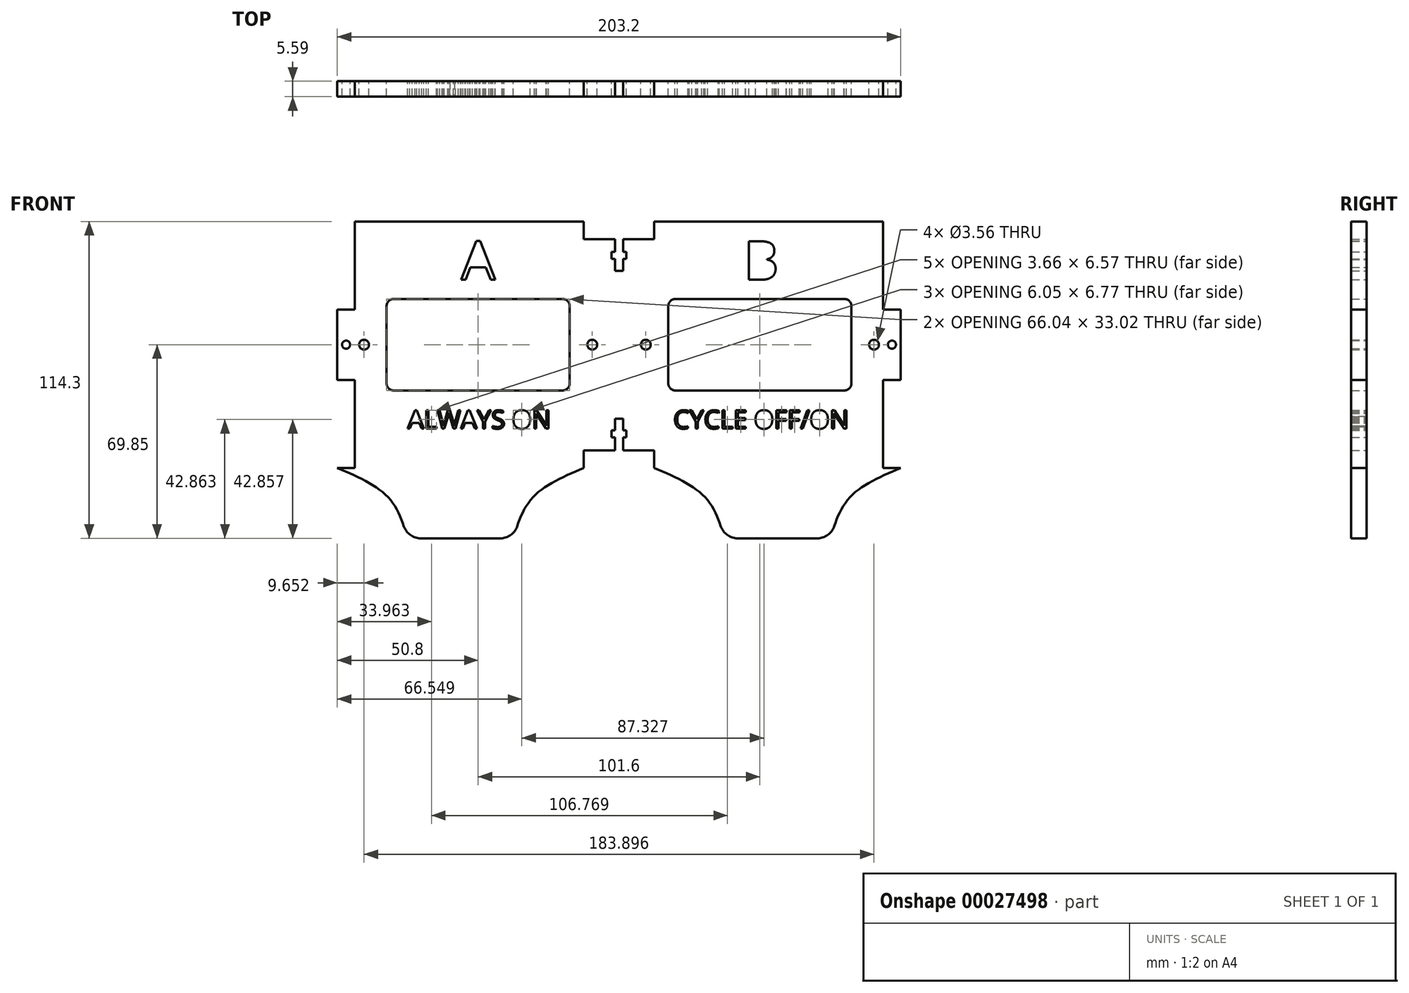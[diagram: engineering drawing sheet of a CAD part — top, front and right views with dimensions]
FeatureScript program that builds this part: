
annotation { "Feature Type Name" : "Feature", "Feature Type Description" : "" }
export const myFeature = defineFeature(function(context is Context, id is Id, definition is map)
    precondition{}
    {
        {
            var Q0;
            Q0=qCreatedBy(makeId("Front.planeOp"),FACE);
            var sketch = newSketch(context, id + "F0", { "sketchPlane" : qUnion([Q0])});
            skLineSegment(sketch, "E0.rect.bottom", {"start": v(95.25, 44.45) * mm, "end": v(12.7, 44.45) * mm});
            skLineSegment(sketch, "E0.rect.left", {"start": v(101.6, 12.7) * mm, "end": v(101.6, -12.7) * mm});
            skPoint(sketch, "E0.rect.middle", {"position": v(0, 0) * mm});
            skLineSegment(sketch, "E1", {"start": v(0, 44.45) * mm, "end": v(0, -44.45) * mm, "construction": true});
            skLineSegment(sketch, "E2", {"start": v(0, 0) * mm, "end": v(95.25, 0) * mm, "construction": true});
            skPoint(sketch, "E3.orphan", {"position": v(-101.6, 0) * mm});
            skLineSegment(sketch, "E4", {"start": v(0, 0) * mm, "end": v(-101.6, 0) * mm, "construction": true});
            skLineSegment(sketch, "E5.rect.bottom", {"start": v(-20.32, -16.51) * mm, "end": v(-81.28, -16.51) * mm});
            skLineSegment(sketch, "E5.rect.top", {"start": v(-20.32, 16.5) * mm, "end": v(-81.28, 16.5) * mm});
            skLineSegment(sketch, "E5.rect.left", {"start": v(-17.78, -13.97) * mm, "end": v(-17.78, 13.97) * mm});
            skLineSegment(sketch, "E5.rect.right", {"start": v(-83.82, -13.97) * mm, "end": v(-83.82, 13.97) * mm});
            skPoint(sketch, "E5.rect.middle", {"position": v(-50.8, 0) * mm});
            skPoint(sketch, "E6.visualSharp", {"position": v(-17.78, 16.51) * mm});
            skArc(sketch, "E6.filletArc", {"start": v(-17.78, 13.97) * mm, "mid": v(-18.52, 15.77) * mm, "end": v(-20.32, 16.5) * mm});
            skPoint(sketch, "E7.visualSharp", {"position": v(-83.82, 16.51) * mm});
            skArc(sketch, "E7.filletArc", {"start": v(-81.28, 16.5) * mm, "mid": v(-83.08, 15.77) * mm, "end": v(-83.82, 13.97) * mm});
            skPoint(sketch, "E8.visualSharp", {"position": v(-83.82, -16.51) * mm});
            skArc(sketch, "E8.filletArc", {"start": v(-83.82, -13.97) * mm, "mid": v(-83.08, -15.77) * mm, "end": v(-81.28, -16.5) * mm});
            skPoint(sketch, "E9.visualSharp", {"position": v(-17.78, -16.51) * mm});
            skArc(sketch, "E9.filletArc", {"start": v(-20.32, -16.51) * mm, "mid": v(-18.52, -15.77) * mm, "end": v(-17.78, -13.97) * mm});
            skCircle(sketch, "E10", {"center": v(-91.95, 0) * mm, "radius": 1.78 * mm});
            skCircle(sketch, "E11", {"center": v(-9.65, 0) * mm, "radius": 1.78 * mm});
            skLineSegment(sketch, "E12.MirrorCS", {"start": v(20.32, 16.5) * mm, "end": v(81.28, 16.5) * mm});
            skLineSegment(sketch, "E13.MirrorCS", {"start": v(83.82, -13.97) * mm, "end": v(83.82, 13.97) * mm});
            skLineSegment(sketch, "E14.MirrorCS", {"start": v(20.32, -16.51) * mm, "end": v(81.28, -16.51) * mm});
            skLineSegment(sketch, "E15.MirrorCS", {"start": v(17.78, -13.97) * mm, "end": v(17.78, 13.97) * mm});
            skCircle(sketch, "E16.MirrorC", {"center": v(9.65, 0) * mm, "radius": 1.78 * mm});
            skCircle(sketch, "E17.MirrorC", {"center": v(91.95, 0) * mm, "radius": 1.78 * mm});
            skArc(sketch, "E18.MirrorCS", {"start": v(20.32, -16.51) * mm, "mid": v(18.52, -15.77) * mm, "end": v(17.78, -13.97) * mm});
            skArc(sketch, "E19.MirrorCS", {"start": v(17.78, 13.97) * mm, "mid": v(18.52, 15.77) * mm, "end": v(20.32, 16.5) * mm});
            skArc(sketch, "E20.MirrorCS", {"start": v(81.28, 16.5) * mm, "mid": v(83.08, 15.77) * mm, "end": v(83.82, 13.97) * mm});
            skArc(sketch, "E21.MirrorCS", {"start": v(83.82, -13.97) * mm, "mid": v(83.08, -15.77) * mm, "end": v(81.28, -16.5) * mm});
            skLineSegment(sketch, "E22", {"start": v(-83.82, 16.51) * mm, "end": v(-101.6, 16.51) * mm, "construction": true});
            skLineSegment(sketch, "E23", {"start": v(-101.6, 12.7) * mm, "end": v(-101.6, -12.7) * mm});
            skLineSegment(sketch, "E24", {"start": v(-12.7, 44.45) * mm, "end": v(-95.25, 44.45) * mm});
            skLineSegment(sketch, "E25", {"start": v(-101.6, 30.48) * mm, "end": v(-50.8, 30.48) * mm, "construction": true});
            skPoint(sketch, "E25.endSnap0", {"position": v(-50.8, 44.45) * mm});
            skText(sketch, "E26", { "text": "A", "fontName": "OpenSans-Regular.ttf"});
            skLineSegment(sketch, "E27", {"start": v(-44.62, 30.45) * mm, "end": v(-56.9, 30.45) * mm, "construction": true});
            skText(sketch, "E28", { "text": "B", "fontName": "OpenSans-Regular.ttf"});
            skLineSegment(sketch, "E29", {"start": v(44.97, 30.45) * mm, "end": v(50.73, 30.45) * mm, "construction": true});
            skLineSegment(sketch, "E30", {"start": v(50.8, 16.5) * mm, "end": v(50.8, 44.45) * mm, "construction": true});
            skText(sketch, "E31", { "text": "ALWAYS ON", "fontName": "OpenSans-Regular.ttf"});
            skText(sketch, "E32", { "text": "CYCLE OFF/ON", "fontName": "OpenSans-Regular.ttf"});
            skLineSegment(sketch, "E33", {"start": v(-50.8, 0) * mm, "end": v(-50.8, -105.5) * mm, "construction": true});
            skLineSegment(sketch, "E34", {"start": v(50.8, -16.51) * mm, "end": v(50.8, -107.38) * mm, "construction": true});
            skLineSegment(sketch, "E35.0", {"start": v(-95.25, 16.51) * mm, "end": v(-95.25, -44.45) * mm, "construction": true});
            skLineSegment(sketch, "E36.0", {"start": v(95.25, 44.45) * mm, "end": v(95.25, 0) * mm, "construction": true});
            skLineSegment(sketch, "E37.0", {"start": v(-12.7, 44.45) * mm, "end": v(-12.7, -44.45) * mm, "construction": true});
            skLineSegment(sketch, "E38.0", {"start": v(12.7, 44.45) * mm, "end": v(12.7, 26.67) * mm, "construction": true});
            skLineSegment(sketch, "E39", {"start": v(-12.7, 44.45) * mm, "end": v(-12.7, 38.1) * mm});
            skLineSegment(sketch, "E40", {"start": v(-12.7, 38.1) * mm, "end": v(-1.46, 38.1) * mm});
            skLineSegment(sketch, "E41", {"start": v(12.7, 38.1) * mm, "end": v(12.7, 44.45) * mm});
            skPoint(sketch, "E42.orphan", {"position": v(0, 44.45) * mm});
            skLineSegment(sketch, "E43.MirrorCS", {"start": v(12.7, -38.1) * mm, "end": v(12.7, -44.45) * mm});
            skLineSegment(sketch, "E44.MirrorCS", {"start": v(-12.7, -38.1) * mm, "end": v(-1.46, -38.1) * mm});
            skLineSegment(sketch, "E45.MirrorCS", {"start": v(-12.7, -44.45) * mm, "end": v(-12.7, -38.1) * mm});
            skLineSegment(sketch, "E46", {"start": v(12.7, 26.67) * mm, "end": v(-12.7, 26.67) * mm, "construction": true});
            skLineSegment(sketch, "E47.0", {"start": v(-1.46, 44.45) * mm, "end": v(-1.46, -44.45) * mm, "construction": true});
            skLineSegment(sketch, "E48.0", {"start": v(1.46, 44.45) * mm, "end": v(1.46, -44.45) * mm, "construction": true});
            skLineSegment(sketch, "E49", {"start": v(-12.7, 32.18) * mm, "end": v(12.7, 32.18) * mm, "construction": true});
            skLineSegment(sketch, "E50", {"start": v(12.7, 26.67) * mm, "end": v(12.7, -44.45) * mm, "construction": true});
            skLineSegment(sketch, "E51", {"start": v(12.7, 26.67) * mm, "end": v(12.7, 26.67) * mm});
            skLineSegment(sketch, "E52.0", {"start": v(-2.7, 44.45) * mm, "end": v(-2.7, -44.45) * mm, "construction": true});
            skLineSegment(sketch, "E53.0", {"start": v(2.7, 44.45) * mm, "end": v(2.7, -44.45) * mm, "construction": true});
            skLineSegment(sketch, "E54.0", {"start": v(-12.7, 30.91) * mm, "end": v(12.7, 30.91) * mm, "construction": true});
            skLineSegment(sketch, "E55.0", {"start": v(-12.7, 33.45) * mm, "end": v(12.7, 33.45) * mm, "construction": true});
            skLineSegment(sketch, "E56", {"start": v(-1.46, 38.1) * mm, "end": v(-1.46, 33.45) * mm});
            skLineSegment(sketch, "E57", {"start": v(-1.46, 33.45) * mm, "end": v(-2.7, 33.45) * mm});
            skLineSegment(sketch, "E58", {"start": v(-2.7, 33.45) * mm, "end": v(-2.7, 30.91) * mm});
            skLineSegment(sketch, "E59", {"start": v(-2.7, 30.91) * mm, "end": v(-1.46, 30.91) * mm});
            skLineSegment(sketch, "E60", {"start": v(-1.46, 30.91) * mm, "end": v(-1.46, 26.67) * mm});
            skLineSegment(sketch, "E61", {"start": v(-1.46, 26.67) * mm, "end": v(1.46, 26.67) * mm});
            skLineSegment(sketch, "E62", {"start": v(1.46, 26.67) * mm, "end": v(1.46, 30.91) * mm});
            skLineSegment(sketch, "E63", {"start": v(1.46, 30.91) * mm, "end": v(2.7, 30.91) * mm});
            skLineSegment(sketch, "E64", {"start": v(2.7, 30.91) * mm, "end": v(2.7, 33.45) * mm});
            skLineSegment(sketch, "E65", {"start": v(2.7, 33.45) * mm, "end": v(1.46, 33.45) * mm});
            skLineSegment(sketch, "E66", {"start": v(1.46, 33.45) * mm, "end": v(1.46, 38.1) * mm});
            skLineSegment(sketch, "E67.trimOffspring", {"start": v(1.46, 38.1) * mm, "end": v(12.7, 38.1) * mm});
            skLineSegment(sketch, "E68.0", {"start": v(-42.75, -69.85) * mm, "end": v(-71.55, -69.85) * mm});
            skLineSegment(sketch, "E69.0", {"start": v(71.55, -69.85) * mm, "end": v(42.75, -69.85) * mm});
            skLineSegment(sketch, "E70", {"start": v(-57.15, -44.45) * mm, "end": v(-57.15, -69.85) * mm, "construction": true});
            skFitSpline(sketch, "E71", {"points": [v(-76.2, -69.85) * mm, v(-83.23, -55.08) * mm, v(-101.6, -44.45) * mm], "startDerivative": vector(-10.5, 34.32) * mm, "endDerivative": vector(-39.67, 16.86) * mm});
            skFitSpline(sketch, "E72.MirrorCS", {"points": [v(-38.1, -69.85) * mm, v(-31.07, -55.08) * mm, v(-12.7, -44.45) * mm], "startDerivative": vector(10.5, 34.32) * mm, "endDerivative": vector(39.67, 16.86) * mm});
            skFitSpline(sketch, "E73.MirrorCS", {"points": [v(38.1, -69.85) * mm, v(31.07, -55.08) * mm, v(12.7, -44.45) * mm], "startDerivative": vector(-10.5, 34.32) * mm, "endDerivative": vector(-39.67, 16.86) * mm});
            skFitSpline(sketch, "E74.MirrorCS", {"points": [v(76.2, -69.85) * mm, v(83.23, -55.08) * mm, v(101.6, -44.45) * mm], "startDerivative": vector(10.5, 34.32) * mm, "endDerivative": vector(39.67, 16.86) * mm});
            skLineSegment(sketch, "E75.MirrorCS", {"start": v(-1.46, -38.1) * mm, "end": v(-1.46, -33.45) * mm});
            skLineSegment(sketch, "E76.MirrorCS", {"start": v(1.46, -33.45) * mm, "end": v(1.46, -38.1) * mm});
            skLineSegment(sketch, "E77.MirrorCS", {"start": v(-1.46, -33.45) * mm, "end": v(-2.7, -33.45) * mm});
            skLineSegment(sketch, "E78.MirrorCS", {"start": v(-2.7, -33.45) * mm, "end": v(-2.7, -30.91) * mm});
            skLineSegment(sketch, "E79.MirrorCS", {"start": v(-2.7, -30.91) * mm, "end": v(-1.46, -30.91) * mm});
            skLineSegment(sketch, "E80.MirrorCS", {"start": v(-1.46, -30.91) * mm, "end": v(-1.46, -26.67) * mm, "construction": true});
            skLineSegment(sketch, "E81.MirrorCS", {"start": v(-1.46, -26.67) * mm, "end": v(1.46, -26.67) * mm});
            skLineSegment(sketch, "E82.MirrorCS", {"start": v(1.46, -26.67) * mm, "end": v(1.46, -30.91) * mm});
            skLineSegment(sketch, "E83.MirrorCS", {"start": v(1.46, -30.91) * mm, "end": v(2.7, -30.91) * mm});
            skLineSegment(sketch, "E84.MirrorCS", {"start": v(2.7, -30.91) * mm, "end": v(2.7, -33.45) * mm, "construction": true});
            skLineSegment(sketch, "E85.MirrorCS", {"start": v(2.7, -33.45) * mm, "end": v(1.46, -33.45) * mm});
            skLineSegment(sketch, "E86.MirrorCS", {"start": v(1.46, -33.45) * mm, "end": v(1.46, -38.1) * mm, "construction": true});
            skLineSegment(sketch, "E87", {"start": v(-1.46, -26.67) * mm, "end": v(-1.46, -30.91) * mm});
            skLineSegment(sketch, "E88", {"start": v(2.7, -30.91) * mm, "end": v(2.7, -33.45) * mm});
            skLineSegment(sketch, "E89.trimOffspring", {"start": v(1.46, -38.1) * mm, "end": v(12.7, -38.1) * mm});
            skLineSegment(sketch, "E90.0", {"start": v(0, 12.7) * mm, "end": v(101.6, 12.7) * mm, "construction": true});
            skLineSegment(sketch, "E91.0", {"start": v(0, -12.7) * mm, "end": v(101.6, -12.7) * mm, "construction": true});
            skLineSegment(sketch, "E92.MirrorCS", {"start": v(0, 12.7) * mm, "end": v(-101.6, 12.7) * mm, "construction": true});
            skLineSegment(sketch, "E93.MirrorCS", {"start": v(0, -12.7) * mm, "end": v(-101.6, -12.7) * mm, "construction": true});
            skLineSegment(sketch, "E94", {"start": v(95.25, 44.45) * mm, "end": v(95.25, 12.7) * mm});
            skLineSegment(sketch, "E95", {"start": v(95.25, 12.7) * mm, "end": v(101.6, 12.7) * mm});
            skLineSegment(sketch, "E96", {"start": v(101.6, -12.7) * mm, "end": v(95.25, -12.7) * mm});
            skLineSegment(sketch, "E97", {"start": v(95.25, -12.7) * mm, "end": v(95.25, -44.45) * mm});
            skLineSegment(sketch, "E98", {"start": v(95.25, -44.45) * mm, "end": v(101.6, -44.45) * mm});
            skPoint(sketch, "E99.orphan", {"position": v(101.6, 44.45) * mm});
            skLineSegment(sketch, "E100", {"start": v(95.25, 0) * mm, "end": v(95.25, -44.45) * mm, "construction": true});
            skLineSegment(sketch, "E101", {"start": v(95.25, 0) * mm, "end": v(101.6, 0) * mm, "construction": true});
            skCircle(sketch, "E102", {"center": v(98.43, 0) * mm, "radius": 1.46 * mm});
            skCircle(sketch, "E103.MirrorC", {"center": v(-98.43, 0) * mm, "radius": 1.46 * mm});
            skLineSegment(sketch, "E104.MirrorCS", {"start": v(-95.25, 44.45) * mm, "end": v(-95.25, 12.7) * mm});
            skLineSegment(sketch, "E105.MirrorCS", {"start": v(-95.25, 12.7) * mm, "end": v(-101.6, 12.7) * mm});
            skLineSegment(sketch, "E106.MirrorCS", {"start": v(-101.6, -12.7) * mm, "end": v(-95.25, -12.7) * mm});
            skLineSegment(sketch, "E107.MirrorCS", {"start": v(-95.25, -12.7) * mm, "end": v(-95.25, -44.45) * mm});
            skLineSegment(sketch, "E108.MirrorCS", {"start": v(-95.25, -44.45) * mm, "end": v(-101.6, -44.45) * mm});
            skPoint(sketch, "E109.orphan", {"position": v(-101.6, 44.45) * mm});
            skPoint(sketch, "E110.orphan", {"position": v(-101.6, 16.51) * mm});
            skArc(sketch, "E111.filletArc", {"start": v(-77.57, -65.55) * mm, "mid": v(-75.25, -68.66) * mm, "end": v(-71.55, -69.85) * mm});
            skArc(sketch, "E112.filletArc", {"start": v(-42.75, -69.85) * mm, "mid": v(-39.05, -68.66) * mm, "end": v(-36.73, -65.55) * mm});
            skArc(sketch, "E113.filletArc", {"start": v(36.73, -65.55) * mm, "mid": v(39.05, -68.66) * mm, "end": v(42.75, -69.85) * mm});
            skArc(sketch, "E114.filletArc", {"start": v(71.55, -69.85) * mm, "mid": v(75.25, -68.66) * mm, "end": v(77.57, -65.55) * mm});
            const initialGuessF0  = {"E26": [-0.0569, 0.02347, 1, 0, 0.01397], "E28": [0.04497, 0.02347, 1, 0, 0.01397], "E31": [-0.0762, -0.03028, 1, 0, 0.00663], "E32": [0.01962, -0.03028, 1, 0, 0.00663]};
            skSetInitialGuess(sketch, initialGuessF0);
            skSolve(sketch);
        }
        {
            var Q0;
            Q0=makeQuery(id+"F0.imprint","IMPRINT",FACE,{"disambiguationData":[TD([[makeQuery(id+"F0.imprint","IMPRINT",EDGE,{"derivedFrom":sQuery(id+"F0.wireOp",EDGE,"E0.rect.bottom")}),1.0]])]});
            extrude(context, id + "F1", {"entities" : qUnion([Q0]), "depth" : 5.6 * mm});
        }
    });
